# Revit family: NBS_DudleyIndustriesLimited_SoapDpnsrs_PlatinumSoapDispenser_375mlFoamSoap
name_source: partatom
category: Furniture
revit_build: Autodesk Revit 2018 (Build: 20190510_1515(x64)
units: mm (PartAtom-declared; Revit-internal decimal feet)

## family parameters
Cut with Voids When Loaded = No
Host = Face
Room Calculation Point = No
Shared = No

## types (1)
- PlatinumSoapDispenser_375mlFoamSoap
    AssetType = Fixed
    BIMObjectName = NBS_DudleyIndustriesLimited_SoapDispensers_PlatinumSoapDispenser_375mlFoamSoap
    Category = Pr_40_70_22_81:Soap dispensers
    Default Elevation = 1050 mm
    Description = 375ml soap dispenser
    DispenserMaterial = NBS_DudleyIndustriesLimited_StainlessSteel_Brushed
    DurationUnit = year
    Features = Easily operated, easy to unlock, innovative coating helps prevent fingerprint marks, easy to wipe clean
    Finish = Brushed with clear lacquer
    IfcExportAs = IfcFurnitureType
    IfcExportType = UNDEFINED
    IsBuiltIn = Yes
    ManufacturerName = Dudley Industries Limited
    ManufacturerURL = www.dudleyindustries.com
    Material = Stainless steel
    MaterialsBody = Stainless steel
    MaterialsFinishAndColour = Brushed with clear lacquer
    ModelNumber = 50006CB
    ModelReference = PlatinumSoapDispenser_375mlFoamSoap
    NBSCertification = www.nationalbimlibrary.com/cert/blqeur2s
    NBSDescription = Soap dispensers
    NBSReference = 45-35-72/358
    Name = SoapDispensers_PlatinumSoapDispenser_375mlFoamSoap_DudleyIndustriesLimited
    NominalDepth = 88 mm  [stored 0.288714 ft]
    NominalHeight = 194 mm  [stored 0.636483 ft]
    NominalLength = 0 mm  [stored 0 ft]
    NominalWidth = 89 mm  [stored 0.291995 ft]
    Operation = Push
    ProductInformation = https://www.dudleyindustries.com
    Shape = Rectangular
    Size = 88 x 194 x 89 mm
    Status = UNSET
    Style = Dispenser
    Uniclass2015Code = Pr_40_70_22_81
    Uniclass2015Title = Soap dispensers
    Uniclass2015Version = Products v1.18
    Version = 1
    WarrantyDescription = 10 Years
    WarrantyDurationUnit = year
    Weight = 0.6 kg

note: [stored X ft] marks values corroborated as IEEE doubles in the binary element streams (Revit-internal decimal feet)

## geometry (parser evidence)
native form markers: Sweep x2
no freeform markers — native parametric forms only
